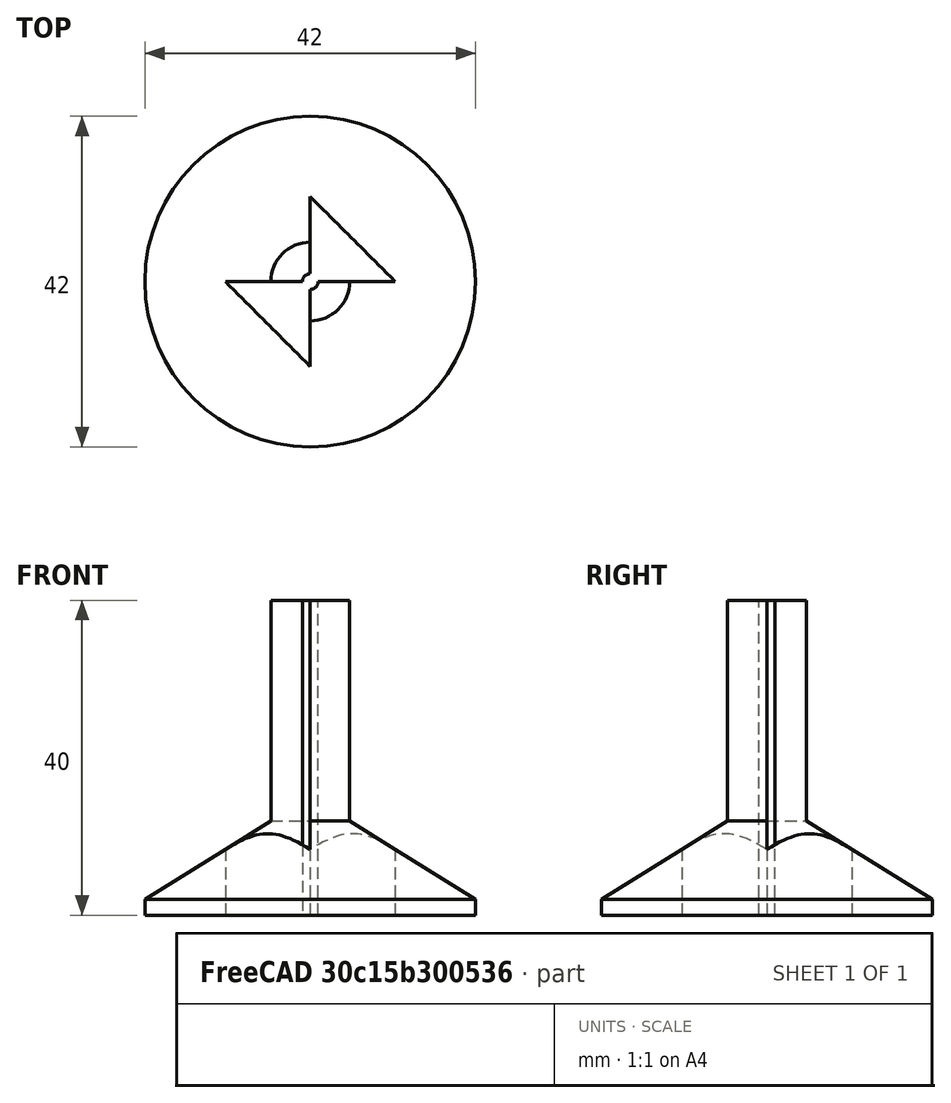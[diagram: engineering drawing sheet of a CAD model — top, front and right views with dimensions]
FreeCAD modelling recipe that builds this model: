
FCSTD DOCUMENT  (FreeCAD 0.19R)
Label: PaintCones
License: All rights reserved
LicenseURL: http://en.wikipedia.org/wiki/All_rights_reserved
objects: Sketcher::SketchObject×3, PartDesign::Pocket×2, PartDesign::Revolution×1, PartDesign::PolarPattern×1, PartDesign::Body×1, Mesh::Feature×1
note: 11 computed .brp shape members not serialized (recipe doc carries the construction recipe); baked Part::Feature solids carry a one-line shape summary decoded from their .brp

FEATURE [Sketcher::SketchObject] Sketch
  FullyConstrained = true
  MapMode = 5
  Placement = pos=(0,0,0) rot=(1,0,0;1.5708rad)
  Support = -> [XZ_Plane]
  sketch-geometry (6):
    g0: LineSegment StartX=0 StartY=0 StartZ=0 EndX=21 EndY=0 EndZ=0
    g1: LineSegment StartX=21 StartY=0 StartZ=0 EndX=21 EndY=2 EndZ=0
    g2: LineSegment StartX=21 StartY=2 StartZ=0 EndX=5 EndY=12 EndZ=0
    g3: LineSegment StartX=5 StartY=12 StartZ=0 EndX=5 EndY=40 EndZ=0
    g4: LineSegment StartX=5 StartY=40 StartZ=0 EndX=0 EndY=40 EndZ=0
    g5: LineSegment StartX=0 StartY=40 StartZ=0 EndX=0 EndY=0 EndZ=0
  constraints (17):
    c: Coincident(g-1,g0)
    c: Horizontal(g0)
    c: Coincident(g0,g1)
    c: Vertical(g1)
    c: Coincident(g1,g2)
    c: Coincident(g2,g3)
    c: Vertical(g3)
    c: Coincident(g3,g4)
    c: PointOnObject(g4,g-2)
    c: Coincident(g4,g5)
    c: Coincident(g5,g0)
    c: DistanceX(g4,g4) = 5
    c: Horizontal(g4)
    c: DistanceX(g0,g0) = 21
    c: Distance(g1) = 2
    c: DistanceY(g2) = 12
    c: DistanceY(g4) = 40
FEATURE [PartDesign::Revolution] Revolution
  Angle = 360
  Axis = (0,2e-16,1)
  Base = (0,0,0)
  Placement = pos=(0,0,0) rot=(1,0,0;1.5708rad)
  Profile = -> Sketch
  ReferenceAxis = -> Sketch [V_Axis]
  Reversed = true
FEATURE [Sketcher::SketchObject] Sketch001
  FullyConstrained = true
  MapMode = 5
  Placement = pos=(0,2.66e-14,40) rot=(0,0,1;3.14159rad)
  Support = -> [Revolution]
  sketch-geometry (3):
    g0: LineSegment StartX=0 StartY=10.79 StartZ=0 EndX=0 EndY=0 EndZ=0
    g1: LineSegment StartX=0 StartY=0 StartZ=0 EndX=10.79 EndY=0 EndZ=0
    g2: LineSegment StartX=10.79 StartY=0 StartZ=0 EndX=0 EndY=10.79 EndZ=0
  constraints (8):
    c: PointOnObject(g0,g-2)
    c: Coincident(g0,g-1)
    c: Coincident(g0,g1)
    c: PointOnObject(g1,g-1)
    c: Coincident(g1,g2)
    c: Equal(g0,g1)
    c: Coincident(g2,g0)
    c: Distance(g1) = 10.79
FEATURE [PartDesign::Pocket] Pocket
  BaseFeature = -> Revolution
  Length = 92
  Length2 = 100
  Placement = pos=(0,0,0) rot=(1,0,0;1.5708rad)
  Profile = -> Sketch001
  Type = 0
FEATURE [PartDesign::PolarPattern] PolarPattern
  Angle = 360
  Axis = -> Sketch001 [N_Axis]
  BaseFeature = -> Pocket
  Occurrences = 2
  Originals = -> [Pocket]
  Placement = pos=(0,0,0) rot=(1,0,0;1.5708rad)
FEATURE [Sketcher::SketchObject] Sketch002
  FullyConstrained = true
  MapMode = 5
  Placement = pos=(0,4.44e-14,40) rot=(0,0,1;3.14159rad)
  Support = -> [PolarPattern]
  sketch-geometry (1):
    g0: Circle CenterX=0 CenterY=0 CenterZ=0 NormalX=0 NormalY=0 NormalZ=1 AngleXU=0 Radius=1
  constraints (2):
    c: Diameter(g0) = 2
    c: Coincident(g0,g-1)
FEATURE [PartDesign::Pocket] Pocket001
  BaseFeature = -> PolarPattern
  Length = 100
  Length2 = 100
  Placement = pos=(0,0,0) rot=(1,0,0;1.5708rad)
  Profile = -> Sketch002
  Type = 0
FEATURE [PartDesign::Body] Body
  Group = -> [Sketch,Revolution,Sketch001,Pocket,PolarPattern,Sketch002,Pocket001]
  Origin = -> Origin
  Tip = -> Pocket001
FEATURE [Mesh::Feature] Mesh  label="Pocket001 (Meshed)"
